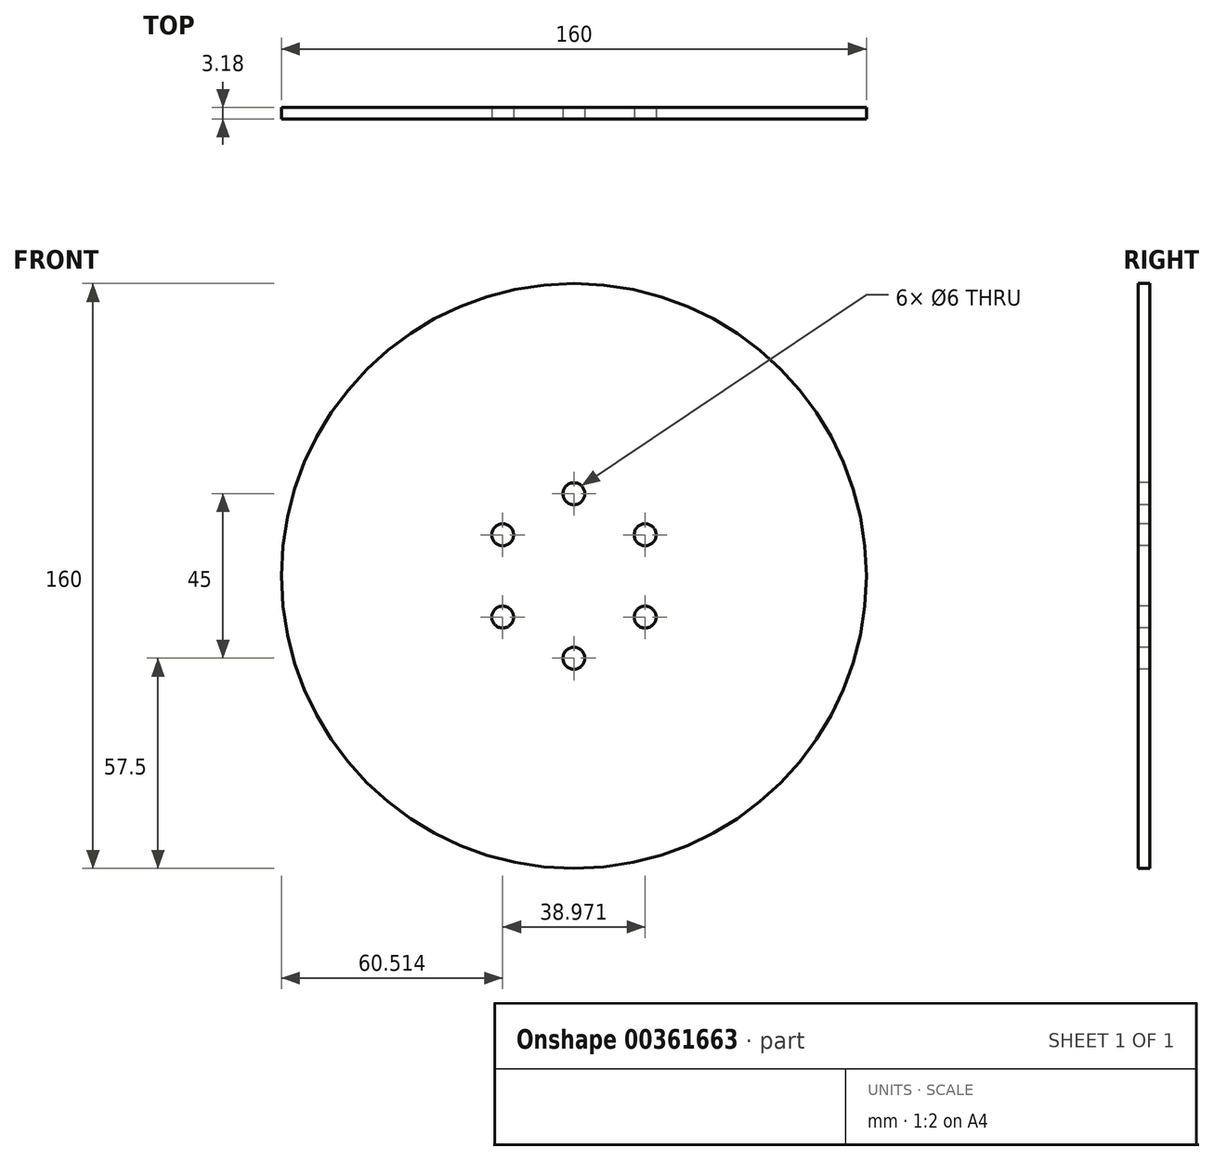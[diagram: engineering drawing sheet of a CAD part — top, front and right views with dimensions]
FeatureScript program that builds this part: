
annotation { "Feature Type Name" : "Feature", "Feature Type Description" : "" }
export const myFeature = defineFeature(function(context is Context, id is Id, definition is map)
    precondition{}
    {
        {
            var Q0;
            Q0=qCreatedBy(makeId("Front.planeOp"),FACE);
            var sketch = newSketch(context, id + "F0", { "sketchPlane" : qUnion([Q0])});
            skCircle(sketch, "E0", {"center": v(0, 0) * mm, "radius": 80 * mm});
            skSolve(sketch);
        }
        {
            var Q0;
            Q0 = qSketchRegion(id + "F0", true);
            extrude(context, id + "F1", {"entities" : qUnion([Q0]), "depth" : 3.17 * mm});
        }
        {
            var Q0;
            Q0=makeQuery(id+"F1.opExtrude","CAP_FACE",FACE,{"disambiguationData":[OSD([sQuery(id+"F0.wireOp",EDGE,"E0")])],"isStart":false});
            var sketch = newSketch(context, id + "F2", { "sketchPlane" : qUnion([Q0])});
            skCircle(sketch, "E1", {"center": v(0, 22.5) * mm, "radius": 3 * mm});
            skCircle(sketch, "E2.1.0", {"center": v(-19.49, 11.25) * mm, "radius": 3 * mm});
            skCircle(sketch, "E2.2.0", {"center": v(-19.49, -11.25) * mm, "radius": 3 * mm});
            skCircle(sketch, "E2.3.0", {"center": v(0, -22.5) * mm, "radius": 3 * mm});
            skCircle(sketch, "E2.4.0", {"center": v(19.49, -11.25) * mm, "radius": 3 * mm});
            skCircle(sketch, "E2.5.0", {"center": v(19.49, 11.25) * mm, "radius": 3 * mm});
            skPoint(sketch, "E2.center", {"position": v(0, 0) * mm});
            skSolve(sketch);
        }
        {
            var Q0;
            Q0 = qSketchRegion(id + "F2", true);
            extrude(context, id + "F3", {"entities" : qUnion([Q0]), "operationType" : NewBodyOperationType.REMOVE, "oppositeDirection" : true, "depth" : 25 * mm, "hasSecondDirection" : true, "secondDirectionOppositeDirection" : false, "secondDirectionDepth" : 25 * mm});
        }
    });
